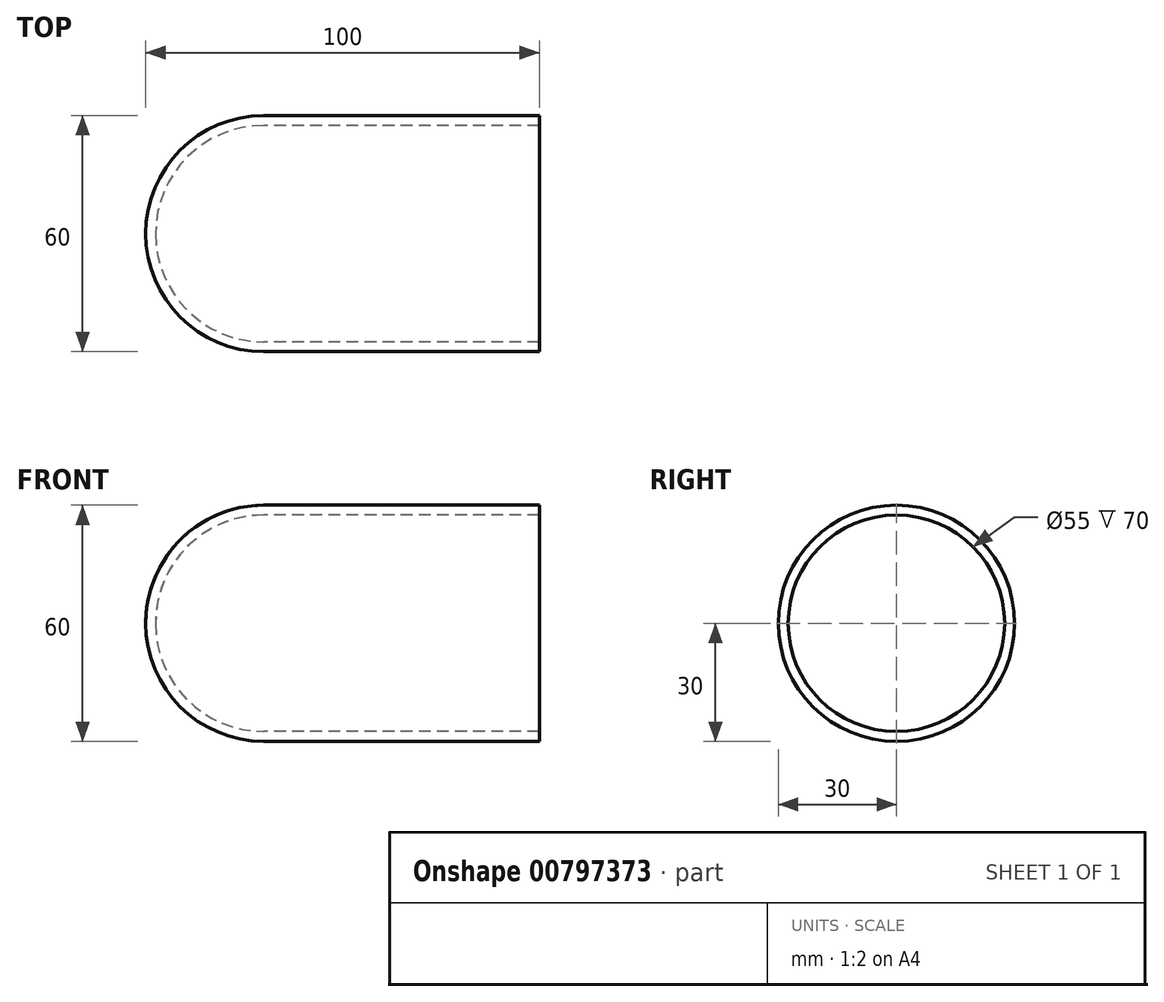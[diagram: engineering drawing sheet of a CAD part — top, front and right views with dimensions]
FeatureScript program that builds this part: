
annotation { "Feature Type Name" : "Feature", "Feature Type Description" : "" }
export const myFeature = defineFeature(function(context is Context, id is Id, definition is map)
    precondition{}
    {
        {
            var Q0;
            Q0=qCreatedBy(makeId("Front.planeOp"),FACE);
            var sketch = newSketch(context, id + "F0", { "sketchPlane" : qUnion([Q0])});
            skLineSegment(sketch, "E0", {"start": v(0, 30) * mm, "end": v(70, 30) * mm});
            skArc(sketch, "E1", {"start": v(0, 30) * mm, "mid": v(-21.21, 21.21) * mm, "end": v(-30, 0) * mm});
            skLineSegment(sketch, "E2", {"start": v(-30, 0) * mm, "end": v(70, 0) * mm, "construction": true});
            skLineSegment(sketch, "E3", {"start": v(-30, 0) * mm, "end": v(70, 0) * mm});
            skLineSegment(sketch, "E4", {"start": v(70, 30) * mm, "end": v(70, 0) * mm});
            skSolve(sketch);
        }
        {
            var Q0;
            Q0=qSketchRegion(id+"F0",true);
            var Q1;
            Q1=sQuery(id+"F0.wireOp",EDGE,"E3");
            revolve(context, id + "F1", {"entities" : qUnion([Q0]), "axis" : qUnion([Q1]), "revolveType" : RevolveType.FULL});
        }
        {
            var Q0;
            Q0=makeQuery(id+"F1.opRevolve","SWEPT_FACE",FACE,{"disambiguationData":[OSD([sQuery(id+"F0.wireOp",EDGE,"E4")])]});
            shell(context, id + "F2", {"entities" : qUnion([Q0]), "thickness" : 2.5 * mm});
        }
    });
